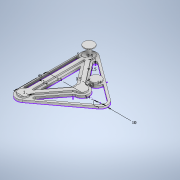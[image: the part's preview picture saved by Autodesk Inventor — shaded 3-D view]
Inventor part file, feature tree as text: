
AUTODESK INVENTOR PART (.ipt)
format: ipt  version: 2022 (Build 260153000, 153)  size: 271,872 bytes
history: native  units: mm
features: extrude x5, sketch x2, fillet x2, other x1
ambient origin geometry x8: Origin, YZ Plane, XZ Plane, XY Plane, X Axis, Y Axis, Z Axis, Center Point
bodies: Body1 (feature_tree)
feature tree (10):
  other  "Sólido1"
  sketch  "Boceto1"  dims[d0=14.0mm d1=45.0mm d2=5.0mm d3=1.0mm d4=10.0mm d5=3.5mm d6=2.0mm d7=3.0mm d8=14.0mm d15=5.0mm d16=0.0mm]
  extrude  "Extrusión2"  Depth=5.0mm TaperAngle=0.0deg
  extrude  "Extrusión3"  Depth=2.0mm
  extrude  "Extrusión4"  Depth=0.5mm
  extrude  "Extrusión5"  Depth=2.0mm
  extrude  "Extrusión6"  Depth=2.5mm
  fillet  "Empalme1"  Radius=2.5mm
  fillet  "Empalme2"  Radius=0.5mm
  sketch  "Boceto2"  dims[d17=15.0mm d18=0.0mm d19=2.0mm d20=0.5mm d21=2.0mm d23=2.5mm d24=2.5mm d25=0.5mm d26=3.0mm d27=0.0mm d28=3.0mm d29=0.0mm d30=14.0mm d31=2.0mm d32=0.0mm d33=2.0mm d34=1.0mm d13=0.5mm d14=0.872665mm]
